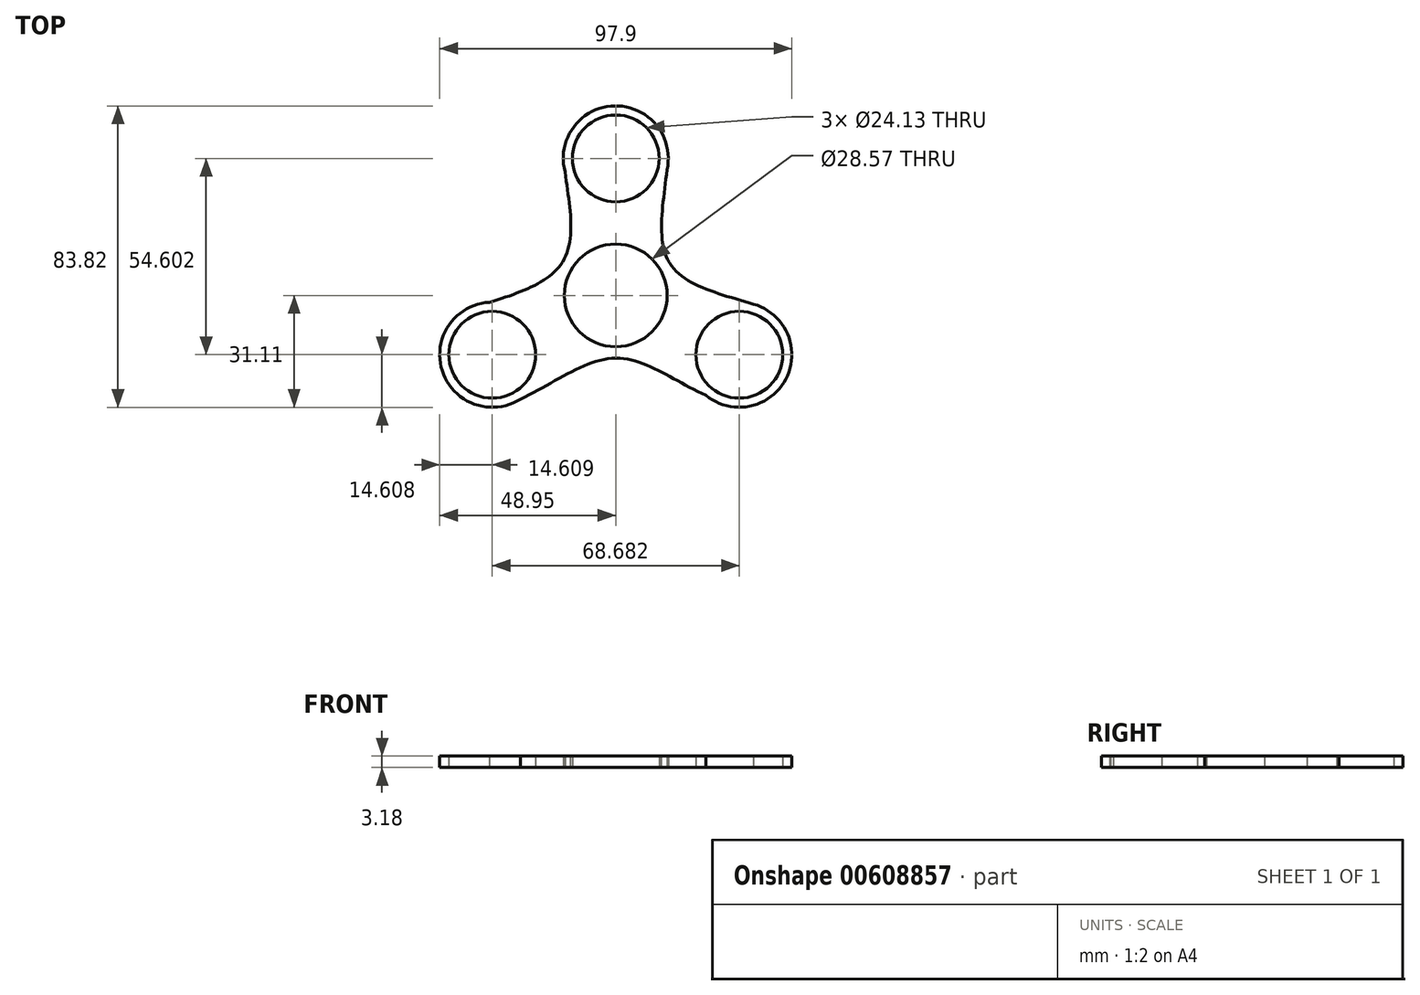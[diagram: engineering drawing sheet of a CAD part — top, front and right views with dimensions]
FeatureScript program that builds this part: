
annotation { "Feature Type Name" : "Feature", "Feature Type Description" : "" }
export const myFeature = defineFeature(function(context is Context, id is Id, definition is map)
    precondition{}
    {
        {
            var Q0;
            Q0=qCreatedBy(makeId("Top.planeOp"),FACE);
            var sketch = newSketch(context, id + "F0", { "sketchPlane" : qUnion([Q0])});
            skCircle(sketch, "E0", {"center": v(0, 0) * mm, "radius": 14.29 * mm});
            skCircle(sketch, "E1.0", {"center": v(0, 0) * mm, "radius": 17.46 * mm});
            skCircle(sketch, "E2", {"center": v(0, 38.1) * mm, "radius": 14.6 * mm});
            skCircle(sketch, "E3", {"center": v(-34.34, -16.5) * mm, "radius": 14.6 * mm});
            skCircle(sketch, "E4.MirrorC", {"center": v(34.34, -16.5) * mm, "radius": 14.6 * mm});
            skLineSegment(sketch, "E5", {"start": v(-14.6, 38.1) * mm, "end": v(14.6, 38.1) * mm});
            skLineSegment(sketch, "E6", {"start": v(34.34, -16.5) * mm, "end": v(43.62, -5.23) * mm});
            skLineSegment(sketch, "E7", {"start": v(43.62, -5.23) * mm, "end": v(25.06, -27.78) * mm});
            skLineSegment(sketch, "E8", {"start": v(-34.34, -16.5) * mm, "end": v(-26.52, -28.83) * mm});
            skLineSegment(sketch, "E9", {"start": v(-26.52, -28.83) * mm, "end": v(-41.86, -3.98) * mm});
            skFitSpline(sketch, "E10", {"points": [v(-26.52, -28.83) * mm, v(0, -17.46) * mm, v(25.06, -27.78) * mm], "startDerivative": vector(55.87, 25.96) * mm, "endDerivative": vector(54.3, -24.52) * mm});
            skFitSpline(sketch, "E11", {"points": [v(14.6, 38.1) * mm, v(15, 8.94) * mm, v(38.3, -2.44) * mm], "startDerivative": vector(-6.36, -64.76) * mm, "endDerivative": vector(57.8, -17.66) * mm});
            skFitSpline(sketch, "E12", {"points": [v(-41.86, -3.98) * mm, v(-14.73, 9.38) * mm, v(-14.6, 38.1) * mm], "startDerivative": vector(64.98, 20.31) * mm, "endDerivative": vector(-7.74, 65.6) * mm});
            skCircle(sketch, "E13.0", {"center": v(0, 38.1) * mm, "radius": 12.06 * mm});
            skCircle(sketch, "E14.0", {"center": v(-34.34, -16.5) * mm, "radius": 12.06 * mm});
            skCircle(sketch, "E15.MirrorC", {"center": v(34.34, -16.5) * mm, "radius": 12.06 * mm});
            skSolve(sketch);
        }
        {
            var Q0;
            {var subQ0=sQuery(id+"F0.wireOp",EDGE,"E11");var subQ1=sQuery(id+"F0.wireOp",EDGE,"E1.0");var subQ2=makeQuery(id+"F0.imprint","INTERSECT",VERTEX,{"disambiguationData":[OD(0.0)],"derivedFrom":[subQ1,subQ0]});Q0=makeQuery(id+"F0.imprint","IMPRINT",FACE,{"disambiguationData":[TD([[makeQuery(id+"F0.imprint","IMPRINT",EDGE,{"disambiguationData":[TD([[subQ2,-1.0]])],"derivedFrom":subQ1}),-1.0]])]});}
            var Q1;
            Q1=makeQuery(id+"F0.imprint","IMPRINT",FACE,{"disambiguationData":[TD([[makeQuery(id+"F0.imprint","IMPRINT",EDGE,{"derivedFrom":sQuery(id+"F0.wireOp",EDGE,"E0")}),-1.0]])]});
            var Q2;
            {var subQ0=sQuery(id+"F0.wireOp",EDGE,"E10");var subQ1=sQuery(id+"F0.wireOp",EDGE,"E1.0");var subQ2=makeQuery(id+"F0.imprint","INTERSECT",VERTEX,{"disambiguationData":[OD(1.0)],"derivedFrom":[subQ1,subQ0]});Q2=makeQuery(id+"F0.imprint","IMPRINT",FACE,{"disambiguationData":[TD([[makeQuery(id+"F0.imprint","IMPRINT",EDGE,{"disambiguationData":[TD([[subQ2,-1.0]])],"derivedFrom":subQ1}),-1.0]])]});}
            var Q3;
            {var subQ0=sQuery(id+"F0.wireOp",EDGE,"E10");var subQ1=sQuery(id+"F0.wireOp",EDGE,"E1.0");var subQ2=makeQuery(id+"F0.imprint","INTERSECT",VERTEX,{"disambiguationData":[OD(0.0)],"derivedFrom":[subQ1,subQ0]});Q3=makeQuery(id+"F0.imprint","IMPRINT",FACE,{"disambiguationData":[TD([[makeQuery(id+"F0.imprint","IMPRINT",EDGE,{"disambiguationData":[TD([[subQ2,1.0]])],"derivedFrom":subQ1}),-1.0]])]});}
            var Q4;
            {var subQ2=sQuery(id+"F0.wireOp",EDGE,"E2");var subQ7=sQuery(id+"F0.wireOp",EDGE,"E12");var subQ10=makeQuery(id+"F0.imprint","INTERSECT",VERTEX,{"derivedFrom":[subQ2,subQ7]});Q4=makeQuery(id+"F0.imprint","IMPRINT",FACE,{"disambiguationData":[TD([[makeQuery(id+"F0.imprint","IMPRINT",EDGE,{"disambiguationData":[TD([[subQ10,-1.0]])],"derivedFrom":subQ2}),1.0]])]});}
            var Q5;
            {var subQ0=sQuery(id+"F0.wireOp",EDGE,"E5");var subQ4=sQuery(id+"F0.wireOp",EDGE,"E13.0");var subQ5=makeQuery(id+"F0.imprint","INTERSECT",VERTEX,{"disambiguationData":[OD(0.0)],"derivedFrom":[subQ0,subQ4]});Q5=makeQuery(id+"F0.imprint","IMPRINT",FACE,{"disambiguationData":[TD([[makeQuery(id+"F0.imprint","IMPRINT",EDGE,{"disambiguationData":[TD([[subQ5,1.0]])],"derivedFrom":subQ4}),-1.0]])]});}
            var Q6;
            {var subQ0=sQuery(id+"F0.wireOp",EDGE,"E7");var subQ1=sQuery(id+"F0.wireOp",EDGE,"E4.MirrorC");var subQ6=makeQuery(id+"F0.imprint","INTERSECT",VERTEX,{"derivedFrom":[subQ1,subQ0]});Q6=makeQuery(id+"F0.imprint","IMPRINT",FACE,{"disambiguationData":[TD([[makeQuery(id+"F0.imprint","IMPRINT",EDGE,{"disambiguationData":[TD([[subQ6,1.0]])],"derivedFrom":subQ1}),-1.0]])]});}
            var Q7;
            {var subQ1=sQuery(id+"F0.wireOp",EDGE,"E9");var subQ5=sQuery(id+"F0.wireOp",EDGE,"E14.0");var subQ8=makeQuery(id+"F0.imprint","INTERSECT",VERTEX,{"disambiguationData":[OD(0.0)],"derivedFrom":[subQ1,subQ5]});Q7=makeQuery(id+"F0.imprint","IMPRINT",FACE,{"disambiguationData":[TD([[makeQuery(id+"F0.imprint","IMPRINT",EDGE,{"disambiguationData":[TD([[subQ8,-1.0]])],"derivedFrom":subQ5}),-1.0]])]});}
            var Q8;
            {var subQ0=sQuery(id+"F0.wireOp",EDGE,"E7");var subQ1=sQuery(id+"F0.wireOp",EDGE,"E4.MirrorC");var subQ2=makeQuery(id+"F0.imprint","INTERSECT",VERTEX,{"derivedFrom":[subQ1,subQ0]});Q8=makeQuery(id+"F0.imprint","IMPRINT",FACE,{"disambiguationData":[TD([[makeQuery(id+"F0.imprint","IMPRINT",EDGE,{"disambiguationData":[TD([[subQ2,-1.0]])],"derivedFrom":subQ0}),1.0]])]});}
            extrude(context, id + "F1", {"entities" : qUnion([Q0, Q1, Q2, Q3, Q4, Q5, Q6, Q7, Q8]), "depth" : 3.17 * mm, "offsetDistance" : 25.4 * mm});
        }
        {
            var Q0;
            Q0 = qSketchRegion(id + "F0", true);
            extrude(context, id + "F2", {"entities" : qUnion([Q0]), "operationType" : NewBodyOperationType.ADD, "depth" : 3.17 * mm, "offsetDistance" : 25.4 * mm});
        }
    });
